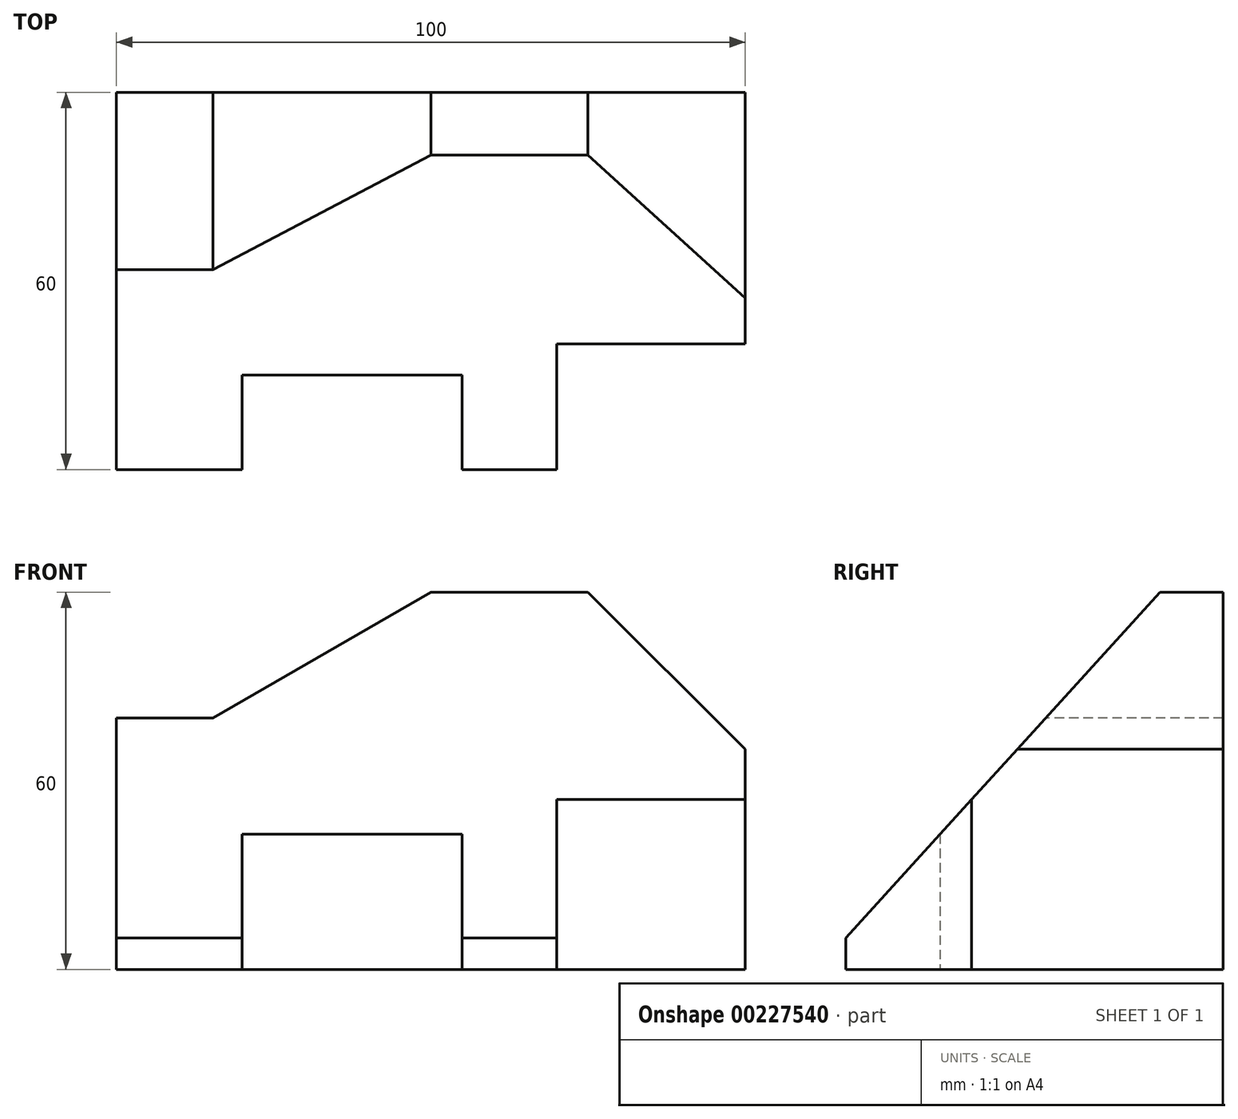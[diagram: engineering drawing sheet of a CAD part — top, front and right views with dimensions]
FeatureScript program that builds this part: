
annotation { "Feature Type Name" : "Feature", "Feature Type Description" : "" }
export const myFeature = defineFeature(function(context is Context, id is Id, definition is map)
    precondition{}
    {
        {
            var Q0;
            Q0=qCreatedBy(makeId("Top.planeOp"),FACE);
            var sketch = newSketch(context, id + "F0", { "sketchPlane" : qUnion([Q0])});
            skLineSegment(sketch, "E0", {"start": v(0, 0) * mm, "end": v(20, 0) * mm});
            skLineSegment(sketch, "E1", {"start": v(20, 0) * mm, "end": v(20, 15) * mm});
            skLineSegment(sketch, "E2", {"start": v(20, 15) * mm, "end": v(55, 15) * mm});
            skLineSegment(sketch, "E3", {"start": v(55, 15) * mm, "end": v(55, 0) * mm});
            skLineSegment(sketch, "E4", {"start": v(55, 0) * mm, "end": v(70, 0) * mm});
            skLineSegment(sketch, "E5", {"start": v(70, 0) * mm, "end": v(70, 20) * mm});
            skLineSegment(sketch, "E6", {"start": v(70, 20) * mm, "end": v(100, 20) * mm});
            skLineSegment(sketch, "E7", {"start": v(100, 20) * mm, "end": v(100, 60) * mm});
            skLineSegment(sketch, "E8", {"start": v(100, 60) * mm, "end": v(0, 60) * mm});
            skLineSegment(sketch, "E9", {"start": v(0, 60) * mm, "end": v(0, 0) * mm});
            skSolve(sketch);
        }
        {
            var Q0;
            Q0=makeQuery(id+"F0.imprint","IMPRINT",FACE,{"disambiguationData":[TD([[makeQuery(id+"F0.imprint","IMPRINT",EDGE,{"derivedFrom":sQuery(id+"F0.wireOp",EDGE,"E0")}),1.0]])]});
            extrude(context, id + "F1", {"entities" : qUnion([Q0]), "depth" : 60 * mm});
        }
        {
            var Q0;
            Q0=qCreatedBy(makeId("Front.planeOp"),FACE);
            var sketch = newSketch(context, id + "F2", { "sketchPlane" : qUnion([Q0])});
            skLineSegment(sketch, "E10", {"start": v(0, 60) * mm, "end": v(98.03, 60) * mm, "construction": true});
            skLineSegment(sketch, "E11", {"start": v(0, 40) * mm, "end": v(15.36, 40) * mm});
            skLineSegment(sketch, "E12", {"start": v(15.36, 40) * mm, "end": v(50, 60) * mm});
            skLineSegment(sketch, "E13", {"start": v(50, 60) * mm, "end": v(0, 60) * mm});
            skLineSegment(sketch, "E14", {"start": v(100, 0) * mm, "end": v(100, 65.64) * mm, "construction": true});
            skLineSegment(sketch, "E15", {"start": v(75, 60) * mm, "end": v(100, 35) * mm});
            skLineSegment(sketch, "E16", {"start": v(0, 40) * mm, "end": v(0, 60) * mm});
            skLineSegment(sketch, "E17", {"start": v(75, 60) * mm, "end": v(100, 60) * mm});
            skLineSegment(sketch, "E18", {"start": v(100, 60) * mm, "end": v(100, 35) * mm});
            skSolve(sketch);
        }
        {
            var Q0;
            Q0 = qSketchRegion(id + "F2", true);
            extrude(context, id + "F3", {"entities" : qUnion([Q0]), "operationType" : NewBodyOperationType.REMOVE, "endBound" : BoundingType.THROUGH_ALL, "oppositeDirection" : true, "depth" : 25 * mm});
        }
        {
            var Q0;
            Q0=qCreatedBy(makeId("Right.planeOp"),FACE);
            var sketch = newSketch(context, id + "F4", { "sketchPlane" : qUnion([Q0])});
            skLineSegment(sketch, "E19", {"start": v(0, 0) * mm, "end": v(0, 5) * mm, "construction": true});
            skLineSegment(sketch, "E20", {"start": v(0, 5) * mm, "end": v(50, 60) * mm});
            skLineSegment(sketch, "E21", {"start": v(50, 60) * mm, "end": v(0, 60) * mm});
            skLineSegment(sketch, "E22", {"start": v(0, 60) * mm, "end": v(0, 5) * mm});
            skSolve(sketch);
        }
        {
            var Q0;
            Q0 = qSketchRegion(id + "F4", true);
            extrude(context, id + "F5", {"entities" : qUnion([Q0]), "operationType" : NewBodyOperationType.REMOVE, "endBound" : BoundingType.THROUGH_ALL, "depth" : 25 * mm});
        }
    });
